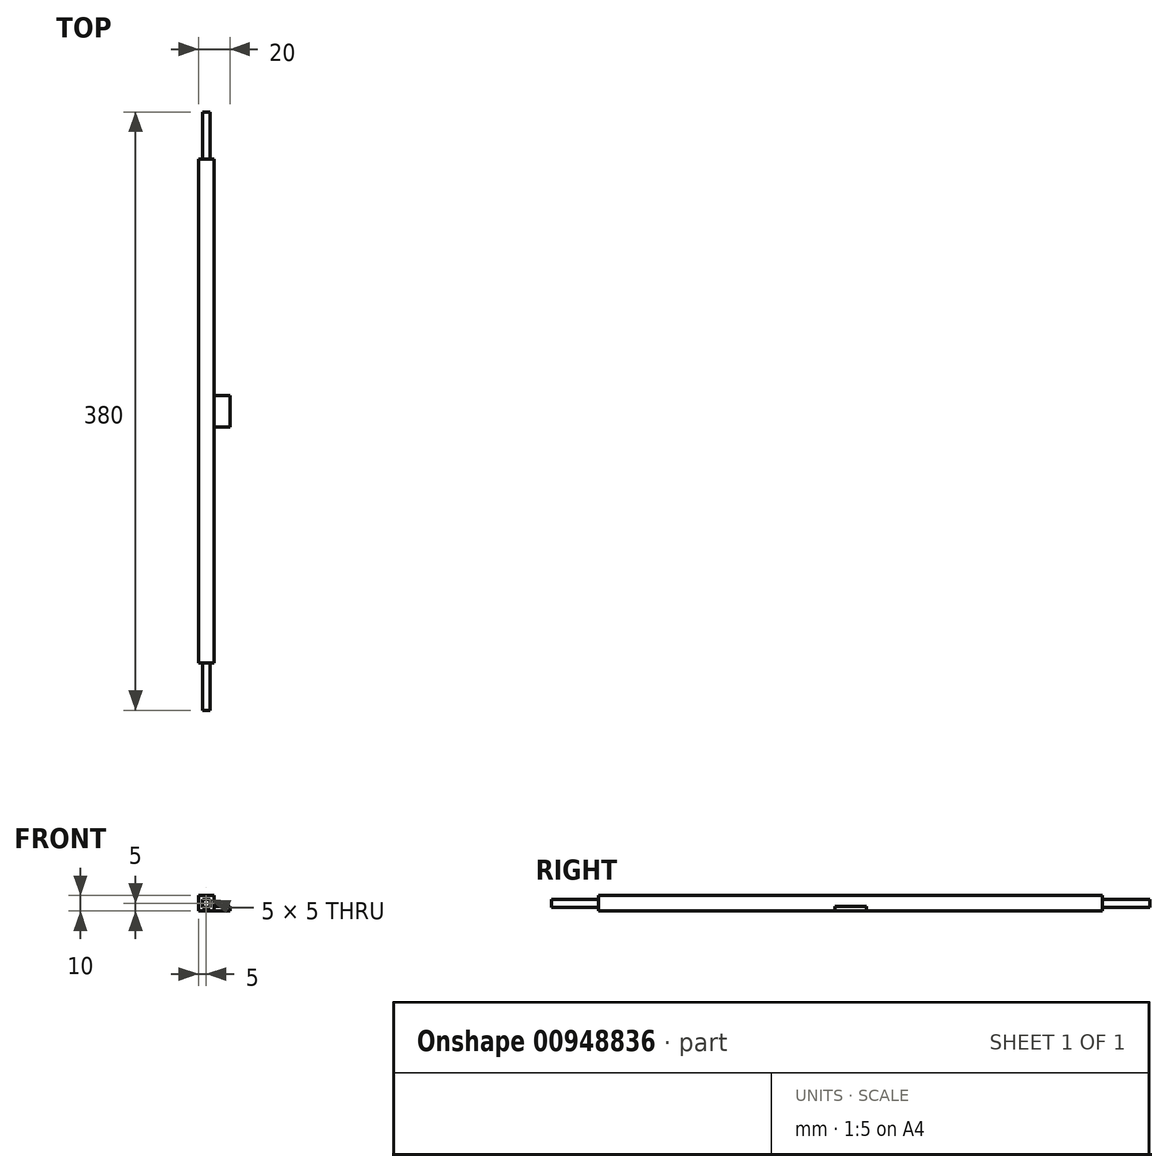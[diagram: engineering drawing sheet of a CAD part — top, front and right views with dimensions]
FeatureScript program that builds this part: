
annotation { "Feature Type Name" : "Feature", "Feature Type Description" : "" }
export const myFeature = defineFeature(function(context is Context, id is Id, definition is map)
    precondition{}
    {
        {
            var Q0;
            Q0=qCreatedBy(makeId("Front.planeOp"),FACE);
            var sketch = newSketch(context, id + "F0", { "sketchPlane" : qUnion([Q0])});
            skLineSegment(sketch, "E0.bottom", {"start": v(5, -5) * mm, "end": v(-5, -5) * mm});
            skLineSegment(sketch, "E0.top", {"start": v(5, 5) * mm, "end": v(-5, 5) * mm});
            skLineSegment(sketch, "E0.left", {"start": v(5, -5) * mm, "end": v(5, 5) * mm});
            skLineSegment(sketch, "E0.right", {"start": v(-5, -5) * mm, "end": v(-5, 5) * mm});
            skPoint(sketch, "E0.middle", {"position": v(0, 0) * mm});
            skSolve(sketch);
        }
        {
            var Q0;
            Q0=qSketchRegion(id+"F0",true);
            extrude(context, id + "F1", {"entities" : qUnion([Q0]), "endBound" : BoundingType.SYMMETRIC, "depth" : 320 * mm, "offsetDistance" : 25 * mm});
        }
        {
            var Q0;
            Q0=makeQuery(id+"F1.opExtrude","SWEPT_FACE",FACE,{"disambiguationData":[OSD([sQuery(id+"F0.wireOp",EDGE,"E0.left")])]});
            var sketch = newSketch(context, id + "F2", { "sketchPlane" : qUnion([Q0])});
            skLineSegment(sketch, "E1.bottom", {"start": v(-10, -5) * mm, "end": v(10, -5) * mm});
            skLineSegment(sketch, "E1.top", {"start": v(-10, -2) * mm, "end": v(10, -2) * mm});
            skLineSegment(sketch, "E1.left", {"start": v(-10, -5) * mm, "end": v(-10, -2) * mm});
            skLineSegment(sketch, "E1.right", {"start": v(10, -5) * mm, "end": v(10, -2) * mm});
            skSolve(sketch);
        }
        {
            var Q0;
            Q0=qSketchRegion(id+"F2",true);
            extrude(context, id + "F3", {"entities" : qUnion([Q0]), "operationType" : NewBodyOperationType.ADD, "depth" : 10 * mm, "offsetDistance" : 25 * mm});
        }
        {
            var Q0;
            Q0=makeQuery(id+"F1.opExtrude","CAP_FACE",FACE,{"disambiguationData":[OSD([sQuery(id+"F0.wireOp",EDGE,"E0.bottom"),sQuery(id+"F0.wireOp",EDGE,"E0.top"),sQuery(id+"F0.wireOp",EDGE,"E0.left"),sQuery(id+"F0.wireOp",EDGE,"E0.right")])],"isStart":false});
            var sketch = newSketch(context, id + "F4", { "sketchPlane" : qUnion([Q0])});
            skLineSegment(sketch, "E2.bottom", {"start": v(2.5, -2.5) * mm, "end": v(-2.5, -2.5) * mm});
            skLineSegment(sketch, "E2.top", {"start": v(2.5, 2.5) * mm, "end": v(-2.5, 2.5) * mm});
            skLineSegment(sketch, "E2.left", {"start": v(2.5, -2.5) * mm, "end": v(2.5, 2.5) * mm});
            skLineSegment(sketch, "E2.right", {"start": v(-2.5, -2.5) * mm, "end": v(-2.5, 2.5) * mm});
            skPoint(sketch, "E2.middle", {"position": v(0, 0) * mm});
            skSolve(sketch);
        }
        {
            var Q0;
            Q0=qSketchRegion(id+"F4",true);
            extrude(context, id + "F5", {"entities" : qUnion([Q0]), "operationType" : NewBodyOperationType.ADD, "depth" : 30 * mm, "offsetDistance" : 25 * mm});
        }
        {
            var Q0;
            Q0=makeQuery(id+"F1.opExtrude","CAP_FACE",FACE,{"disambiguationData":[OSD([sQuery(id+"F0.wireOp",EDGE,"E0.bottom"),sQuery(id+"F0.wireOp",EDGE,"E0.top"),sQuery(id+"F0.wireOp",EDGE,"E0.left"),sQuery(id+"F0.wireOp",EDGE,"E0.right")])],"isStart":true});
            var sketch = newSketch(context, id + "F6", { "sketchPlane" : qUnion([Q0])});
            skLineSegment(sketch, "E3.bottom", {"start": v(2.5, -2.5) * mm, "end": v(-2.5, -2.5) * mm});
            skLineSegment(sketch, "E3.top", {"start": v(2.5, 2.5) * mm, "end": v(-2.5, 2.5) * mm});
            skLineSegment(sketch, "E3.left", {"start": v(2.5, -2.5) * mm, "end": v(2.5, 2.5) * mm});
            skLineSegment(sketch, "E3.right", {"start": v(-2.5, -2.5) * mm, "end": v(-2.5, 2.5) * mm});
            skPoint(sketch, "E3.middle", {"position": v(0, 0) * mm});
            skSolve(sketch);
        }
        {
            var Q0;
            Q0=qSketchRegion(id+"F6",true);
            extrude(context, id + "F7", {"entities" : qUnion([Q0]), "operationType" : NewBodyOperationType.ADD, "depth" : 30 * mm, "offsetDistance" : 25 * mm});
        }
    });
